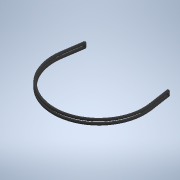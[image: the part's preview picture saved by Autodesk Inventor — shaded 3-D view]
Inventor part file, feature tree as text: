
AUTODESK INVENTOR PART (.ipt)
format: ipt  version: 2020.3 (Build 243373000, 373)  size: 284,672 bytes
history: native  units: mm
features: sketch x7, plane x6, fillet x6, extrude x3, sweep x2
ambient origin geometry x8: Origin, YZ Plane, XZ Plane, XY Plane, X Axis, Y Axis, Z Axis, Center Point
bodies: Solid1 (feature_tree), Solid2 (feature_tree)
feature tree (24):
  sketch  "Sketch1"  dims[d0=92.6mm d1=1.3mm d2=1.3mm d3=45.792087mm d4=6.839208mm d5=1.3mm d6=1.3mm d7=45.792087mm d8=2.6mm]
  plane  "Work Plane1"
  sweep  "Sweep1"
  plane  "Work Plane2"
  sketch  "Sketch3"  dims[d12=92.6mm d13=1.3mm d14=1.3mm d15=45.792087mm d16=6.839208mm d17=1.3mm d18=1.3mm d19=45.792087mm d20=2.6mm d21=0.0mm d22=0.0mm]
  plane  "Work Plane3"
  sweep  "Sweep2"
  plane  "Work Plane5"
  extrude  "Extrusion1"  Depth=2.6mm
  fillet  "Fillet1"  [1 undecoded]
  plane  "Work Plane6"
  extrude  "Extrusion2"  Depth=2.6mm
  plane  "Work Plane7"
  extrude  "Extrusion3"  Depth=6.2mm TaperAngle=0.0deg
  fillet  "Fillet2"  Radius=0.5mm
  fillet  "Fillet3"  Radius=2.7mm
  fillet  "Fillet4"  [1 undecoded]
  fillet  "Fillet5"  Radius=2.7mm
  fillet  "Fillet6"  Radius=1.3mm
  sketch  "Sketch2"  dims[d9=0.0mm d10=0.0mm d11=-3.6mm]
  sketch  "Sketch4"  dims[d30=1.3mm d31=2.6mm]
  sketch  "Sketch7"  dims[d32=2.6mm d33=6.2mm d34=0.0mm d35=0.5mm d36=2.7mm d37=0.0mm d38=90.0deg d39=2.7mm d40=0.0mm d41=1.3mm]
  sketch  "Sketch8"  dims[d42=1.3mm]
  sketch  "Sketch9"  dims[d43=1.2mm d44=1.2mm d45=0.6mm d28=0.5mm d29=0.872665mm]
note: 2 required parameter values undecoded (feature->parameter linkage not recoverable at this tier; creation-order binding heuristic only, values carry confidence <= 0.55)
